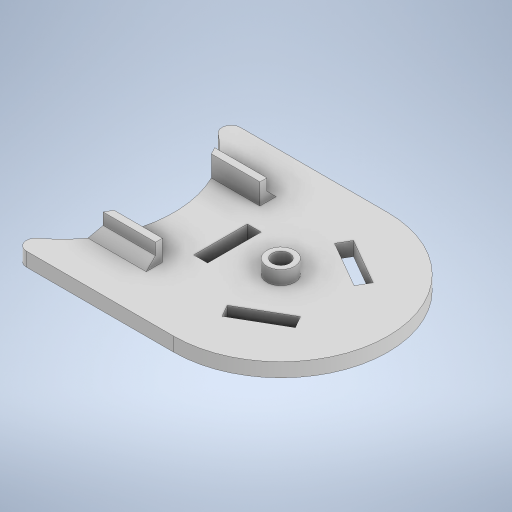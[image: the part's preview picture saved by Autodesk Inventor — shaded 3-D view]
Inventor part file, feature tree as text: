
AUTODESK INVENTOR PART (.ipt)
format: ipt  version: 2024.1 (Build 281209000, 209)  size: 317,952 bytes
history: native  units: mm
features: extrude x7, sketch x7, other x1, fillet x1, chamfer x1
ambient origin geometry x8: Origin, YZ Plane, XZ Plane, XY Plane, X Axis, Y Axis, Z Axis, Center Point
bodies: Body1 (feature_tree)
feature tree (17):
  other  "ソリッド1"
  extrude  "押し出し1"  Depth=12.0mm
  extrude  "押し出し2"  Depth=1.0mm TaperAngle=0.0deg
  extrude  "押し出し3"  Depth=6.0mm
  extrude  "押し出し4"  Depth=3.0mm TaperAngle=0.0deg
  extrude  "押し出し5"  Depth=3.8mm
  fillet  "フィレット1"  [1 undecoded]
  extrude  "押し出し6"  Depth=47.1mm
  extrude  "押し出し7"  Depth=3.0mm TaperAngle=0.0deg
  chamfer  "面取り1"  Distance=0.5mm
  sketch  "スケッチ1"
  sketch  "スケッチ2"
  sketch  "スケッチ3"
  sketch  "スケッチ4"
  sketch  "スケッチ5"
  sketch  "スケッチ6"
  sketch  "スケッチ7"
note: 1 required parameter value undecoded (feature->parameter linkage not recoverable at this tier; creation-order binding heuristic only, values carry confidence <= 0.55)
